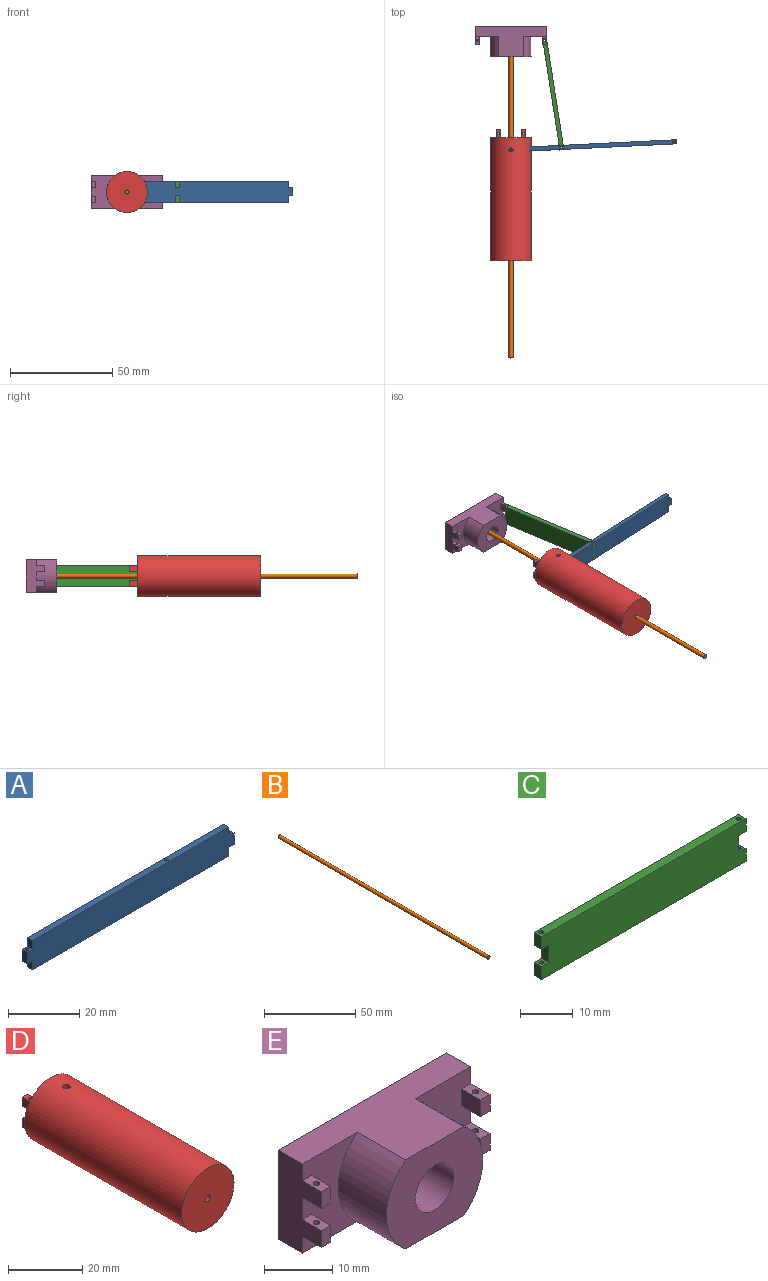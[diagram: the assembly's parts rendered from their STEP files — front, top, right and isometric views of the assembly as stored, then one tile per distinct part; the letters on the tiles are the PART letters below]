
ASSEMBLY  parts=5 mates=5
PART A: 17 faces, bbox 82x2x10 mm
  f0: plane 4x2mm, normal (-1,0,0), area 8mm2, adj f1,f2,f3,f4
  f1: plane 2x2mm, normal (0,0,-1), area 3.2mm2, adj f0,f3,f4,f5,f6
  f2: plane 2x2mm, normal (0,0,1), area 3.2mm2, adj f0,f3,f4,f5,f8
  f3: plane 82x10mm, normal (0,-1,0), area 796mm2, adj f0,f1,f2,f6,f7,f8,f9,f10
  f4: plane 82x10mm, normal (0,1,0), area 796mm2, adj f0,f1,f2,f6,f7,f8,f9,f10
  f5: cylinder r=0.5mm len=4mm, axis (0,0,-1), area 12.6mm2, adj f1,f2
  f6: plane 3x2mm, normal (-1,0,0), area 6mm2, adj f1,f3,f4,f9
  f7: plane 78x2mm, normal (0,0,1), area 155.2mm2, adj f3,f4,f8,f14,f16
  f8: plane 3x2mm, normal (-1,0,0), area 6mm2, adj f2,f3,f4,f7
  f9: plane 78x2mm, normal (0,0,-1), area 155.2mm2, adj f3,f4,f6,f10,f16
  f10: plane 3x2mm, normal (1,0,0), area 6mm2, adj f3,f4,f9,f11
  f11: plane 2x2mm, normal (0,0,-1), area 3.2mm2, adj f3,f4,f10,f12,f15
  f12: plane 4x2mm, normal (1,0,0), area 8mm2, adj f3,f4,f11,f13
  f13: plane 2x2mm, normal (0,0,1), area 3.2mm2, adj f3,f4,f12,f14,f15
  f14: plane 3x2mm, normal (1,0,0), area 6mm2, adj f3,f4,f7,f13
  f15: cylinder r=0.5mm len=4mm, axis (0,0,-1), area 12.6mm2, adj f11,f13
  f16: cylinder r=0.5mm len=10mm, axis (0,0,1), area 31.4mm2, adj f7,f9
PART B: 3 faces, bbox 2x162x2 mm
  f0: cylinder r=1mm len=162mm, axis (0,-1,0), area 1017.9mm2, adj f1,f2
  f1: plane 2x2mm, normal (0,-1,0), area 3.1mm2, adj f0
  f2: plane 2x2mm, normal (0,1,0), area 3.1mm2, adj f0
PART C: 18 faces, bbox 55x2x10 mm
  f0: plane 3x2mm, normal (1,0,0), area 6mm2, adj f1,f11,f12,f13
  f1: plane 2x2mm, normal (0,0,1), area 3.2mm2, adj f0,f2,f12,f13,f14
  f2: plane 4x2mm, normal (1,0,0), area 8mm2, adj f1,f3,f12,f13
  f3: plane 2x2mm, normal (0,0,-1), area 3.2mm2, adj f2,f4,f12,f13,f15
  f4: plane 3x2mm, normal (1,0,0), area 6mm2, adj f3,f5,f12,f13
  f5: plane 55x2mm, normal (0,0,1), area 108.4mm2, adj f4,f6,f12,f13,f15,f17
  f6: plane 3x2mm, normal (-1,0,0), area 6mm2, adj f5,f7,f12,f13
  f7: plane 2x2mm, normal (0,0,-1), area 3.2mm2, adj f6,f8,f12,f13,f17
  f8: plane 4x2mm, normal (-1,0,0), area 8mm2, adj f7,f9,f12,f13
  f9: plane 2x2mm, normal (0,0,1), area 3.2mm2, adj f8,f10,f12,f13,f16
  f10: plane 3x2mm, normal (-1,0,0), area 6mm2, adj f9,f11,f12,f13
  f11: plane 55x2mm, normal (0,0,-1), area 108.4mm2, adj f0,f10,f12,f13,f14,f16
  f12: plane 55x10mm, normal (0,-1,0), area 534mm2, adj f0,f1,f2,f3,f4,f5,f6,f7
  f13: plane 55x10mm, normal (0,1,0), area 534mm2, adj f0,f1,f2,f3,f4,f5,f6,f7
  f14: cylinder r=0.5mm len=3mm, axis (0,0,-1), area 9.4mm2, adj f1,f11
  f15: cylinder r=0.5mm len=3mm, axis (0,0,-1), area 9.4mm2, adj f3,f5
  f16: cylinder r=0.5mm len=3mm, axis (0,0,-1), area 9.4mm2, adj f9,f11
  f17: cylinder r=0.5mm len=3mm, axis (0,0,-1), area 9.4mm2, adj f5,f7
PART D: 31 faces, bbox 20x64x20 mm
  f0: cylinder r=1mm len=6mm, axis (0,-1,0), area 33.7mm2, adj f1,f29,f30
  f1: plane 20x20mm, normal (0,1,0), area 287mm2, adj f0,f3,f5,f6,f7,f8,f10,f11
  f2: cylinder r=1mm len=54mm, axis (0,-1,0), area 335.3mm2, adj f4,f29,f30
  f3: cylinder r=10mm len=60mm, axis (0,-1,0), area 3763.6mm2, adj f1,f4,f29,f30
  f4: plane 20x20mm, normal (0,-1,0), area 311mm2, adj f2,f3
  f5: plane 4x2mm, normal (0,0,-1), area 7.2mm2, adj f1,f6,f8,f9,f28
  f6: plane 4x3mm, normal (1,0,0), area 12mm2, adj f1,f5,f7,f9
  f7: plane 4x2mm, normal (0,0,1), area 7.2mm2, adj f1,f6,f8,f9,f28
  f8: plane 4x3mm, normal (-1,0,0), area 12mm2, adj f1,f5,f7,f9
  f9: plane 3x2mm, normal (0,1,0), area 6mm2, adj f5,f6,f7,f8
  f10: plane 4x3mm, normal (-1,0,0), area 12mm2, adj f1,f11,f13,f14
  f11: plane 4x2mm, normal (0,0,-1), area 7.2mm2, adj f1,f10,f12,f14,f27
  f12: plane 4x3mm, normal (1,0,0), area 12mm2, adj f1,f11,f13,f14
  f13: plane 4x2mm, normal (0,0,1), area 7.2mm2, adj f1,f10,f12,f14,f27
  f14: plane 3x2mm, normal (0,1,0), area 6mm2, adj f10,f11,f12,f13
  f15: plane 4x2mm, normal (0,0,-1), area 7.2mm2, adj f1,f16,f18,f19,f26
  f16: plane 4x3mm, normal (1,0,0), area 12mm2, adj f1,f15,f17,f19
  f17: plane 4x2mm, normal (0,0,1), area 7.2mm2, adj f1,f16,f18,f19,f26
  f18: plane 4x3mm, normal (-1,0,0), area 12mm2, adj f1,f15,f17,f19
  f19: plane 3x2mm, normal (0,1,0), area 6mm2, adj f15,f16,f17,f18
  f20: plane 4x2mm, normal (0,0,-1), area 7.2mm2, adj f1,f21,f23,f24,f25
  f21: plane 4x3mm, normal (1,0,0), area 12mm2, adj f1,f20,f22,f24
  f22: plane 4x2mm, normal (0,0,1), area 7.2mm2, adj f1,f21,f23,f24,f25
  f23: plane 4x3mm, normal (-1,0,0), area 12mm2, adj f1,f20,f22,f24
  f24: plane 3x2mm, normal (0,1,0), area 6mm2, adj f20,f21,f22,f23
  f25: cylinder r=0.5mm len=3mm, axis (0,0,-1), area 9.4mm2, adj f20,f22
  f26: cylinder r=0.5mm len=3mm, axis (0,0,-1), area 9.4mm2, adj f15,f17
  f27: cylinder r=0.5mm len=3mm, axis (0,0,-1), area 9.4mm2, adj f11,f13
  f28: cylinder r=0.5mm len=3mm, axis (0,0,-1), area 9.4mm2, adj f5,f7
  f29: cylinder r=1mm len=10mm, axis (0,0,1), area 58.7mm2, adj f0,f2,f3
  f30: cylinder r=1mm len=10mm, axis (0,0,1), area 58.7mm2, adj f0,f2,f3
PART E: 33 faces, bbox 35x15x16 mm
  f0: cylinder r=1mm len=5mm, axis (0,-1,0), area 31.4mm2, adj f1,f2
  f1: plane 8x8mm, normal (0,-1,0), area 47.1mm2, adj f0,f6
  f2: plane 35x16mm, normal (0,1,0), area 556.9mm2, adj f0,f3,f5,f13,f20
  f3: plane 35x15mm, normal (0,0,1), area 295mm2, adj f2,f4,f7,f8,f9,f10,f13,f20
  f4: cylinder r=10mm len=16mm, axis (0,-1,0), area 185.5mm2, adj f3,f5,f8,f9
  f5: plane 35x15mm, normal (0,0,-1), area 295mm2, adj f2,f4,f7,f8,f9,f10,f13,f20
  f6: cylinder r=4mm len=10mm, axis (0,-1,0), area 251.3mm2, adj f1,f8
  f7: cylinder r=10mm len=16mm, axis (0,-1,0), area 185.5mm2, adj f3,f5,f8,f10
  f8: plane 20x16mm, normal (0,-1,0), area 231.2mm2, adj f3,f4,f5,f6,f7
  f9: plane 16x11.5mm, normal (0,-1,0), area 127.3mm2, adj f3,f4,f5,f11,f12,f13,f14,f16
  f10: plane 16x11.5mm, normal (0,-1,0), area 127.3mm2, adj f3,f5,f7,f20,f21,f22,f23,f25
  f11: plane 4x3mm, normal (1,0,0), area 12mm2, adj f9,f12,f14,f15
  f12: plane 4x2mm, normal (0,0,1), area 7.2mm2, adj f9,f11,f13,f15,f30
  f13: plane 16x9mm, normal (-1,0,0), area 104mm2, adj f2,f3,f5,f9,f12,f14,f15,f17
  f14: plane 4x2mm, normal (0,0,-1), area 7.2mm2, adj f9,f11,f13,f15,f30
  f15: plane 3x2mm, normal (0,-1,0), area 6mm2, adj f11,f12,f13,f14
  f16: plane 4x3mm, normal (1,0,0), area 12mm2, adj f9,f17,f18,f19
  f17: plane 4x2mm, normal (0,0,1), area 7.2mm2, adj f9,f13,f16,f19,f29
  f18: plane 4x2mm, normal (0,0,-1), area 7.2mm2, adj f9,f13,f16,f19,f29
  f19: plane 3x2mm, normal (0,-1,0), area 6mm2, adj f13,f16,f17,f18
  f20: plane 16x9mm, normal (1,0,0), area 104mm2, adj f2,f3,f5,f10,f21,f23,f24,f25
  f21: plane 4x2mm, normal (0,0,1), area 7.2mm2, adj f10,f20,f22,f24,f32
  f22: plane 4x3mm, normal (-1,0,0), area 12mm2, adj f10,f21,f23,f24
  f23: plane 4x2mm, normal (0,0,-1), area 7.2mm2, adj f10,f20,f22,f24,f32
  f24: plane 3x2mm, normal (0,-1,0), area 6mm2, adj f20,f21,f22,f23
  f25: plane 4x2mm, normal (0,0,1), area 7.2mm2, adj f10,f20,f26,f28,f31
  f26: plane 4x3mm, normal (-1,0,0), area 12mm2, adj f10,f25,f27,f28
  f27: plane 4x2mm, normal (0,0,-1), area 7.2mm2, adj f10,f20,f26,f28,f31
  f28: plane 3x2mm, normal (0,-1,0), area 6mm2, adj f20,f25,f26,f27
  f29: cylinder r=0.5mm len=3mm, axis (0,0,-1), area 9.4mm2, adj f17,f18
  f30: cylinder r=0.5mm len=3mm, axis (0,0,-1), area 9.4mm2, adj f12,f14
  f31: cylinder r=0.5mm len=3mm, axis (0,0,-1), area 9.4mm2, adj f25,f27
  f32: cylinder r=0.5mm len=3mm, axis (0,0,-1), area 9.4mm2, adj f21,f23
PLACE A rot(axis=(0,0,-1),177.2deg) t=(-19.47,-8.81,-51.49)mm
PLACE B t=(-43.32,76.92,-21.55)mm
PLACE C rot(axis=(0,0,-1),81.1deg) t=(29.21,-86.64,-21.49)mm
PLACE D t=(-13.72,22.48,-21.55)mm fixed
PLACE E t=(-13.72,51.92,-21.55)mm
MATE cylindrical C.f16 <-> E.f31  axis (0,0,-1) through (2.78,49.92,-16.49)mm
MATE fastened B.f0 <-> E.f0  axis (0,1,0) through (-13.72,56.92,-21.55)mm
MATE revolute C.f14 <-> A.f16  axis (0,0,-1) through (10.97,-2.45,-16.49)mm
MATE revolute A.f15 <-> D.f29  axis (0,0,1) through (-13.72,-3.52,-19.49)mm
MATE slider B.f0 <-> D.f0  axis (0,-1,0) through (-13.72,-105.08,-21.55)mm
